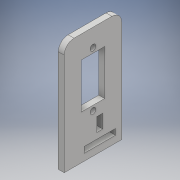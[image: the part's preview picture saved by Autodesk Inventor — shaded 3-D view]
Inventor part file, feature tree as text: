
AUTODESK INVENTOR PART (.ipt)
format: ipt  version: 2018 (Build 220112000, 112)  size: 116,736 bytes
history: native  units: mm
features: other x1, extrude x1, sketch x1
ambient origin geometry x8: Origin, YZ Plane, XZ Plane, XY Plane, X Axis, Y Axis, Z Axis, Center Point
bodies: Body1 (feature_tree)
feature tree (3):
  other  "Sólido1"
  extrude  "Extrusión1"  Depth=5.0mm
  sketch  "Boceto1"  dims[d26=3.0mm d27=0.0mm d28=5.0mm]
